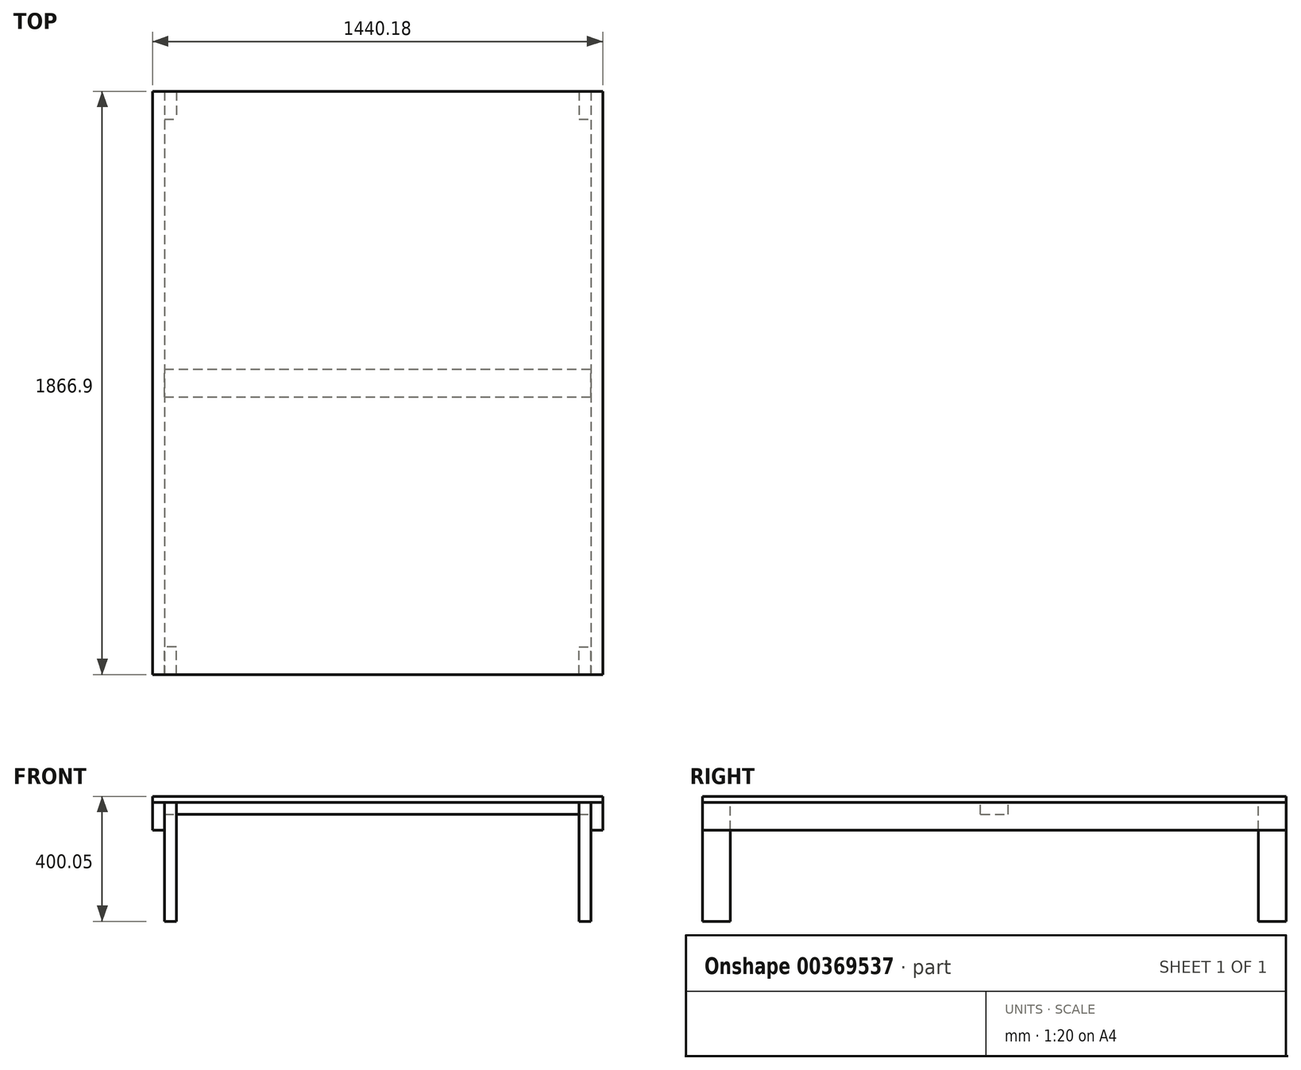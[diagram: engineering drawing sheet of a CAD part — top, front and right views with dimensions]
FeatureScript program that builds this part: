
annotation { "Feature Type Name" : "Feature", "Feature Type Description" : "" }
export const myFeature = defineFeature(function(context is Context, id is Id, definition is map)
    precondition{}
    {
        {
            var Q0;
            Q0=qCreatedBy(makeId("Top.planeOp"),FACE);
            var sketch = newSketch(context, id + "F0", { "sketchPlane" : qUnion([Q0])});
            skLineSegment(sketch, "E0.bottom", {"start": v(-720.1, 933.45) * mm, "end": v(720.1, 933.45) * mm});
            skLineSegment(sketch, "E0.top", {"start": v(-720.1, -933.45) * mm, "end": v(720.09, -933.45) * mm});
            skLineSegment(sketch, "E0.left", {"start": v(-720.1, 933.45) * mm, "end": v(-720.1, -933.45) * mm});
            skLineSegment(sketch, "E0.right", {"start": v(720.1, 933.45) * mm, "end": v(720.09, -933.45) * mm});
            skPoint(sketch, "E0.middle", {"position": v(0, 0) * mm});
            skSolve(sketch);
        }
        {
            var Q0;
            Q0 = qSketchRegion(id + "F0", true);
            extrude(context, id + "F1", {"entities" : qUnion([Q0]), "depth" : 19.05 * mm});
        }
        {
            var Q0;
            Q0=makeQuery(id+"F1.opExtrude","SWEPT_FACE",FACE,{"disambiguationData":[OSD([sQuery(id+"F0.wireOp",EDGE,"E0.top")])]});
            var sketch = newSketch(context, id + "F2", { "sketchPlane" : qUnion([Q0])});
            skLineSegment(sketch, "E1.bottom", {"start": v(720.09, 0) * mm, "end": v(681.99, 0) * mm});
            skLineSegment(sketch, "E1.top", {"start": v(720.09, -88.9) * mm, "end": v(681.99, -88.9) * mm});
            skLineSegment(sketch, "E1.left", {"start": v(720.09, 0) * mm, "end": v(720.09, -88.9) * mm});
            skLineSegment(sketch, "E1.right", {"start": v(681.99, 0) * mm, "end": v(681.99, -88.9) * mm});
            skLineSegment(sketch, "E2.bottom", {"start": v(-720.1, 0) * mm, "end": v(-682, 0) * mm});
            skLineSegment(sketch, "E2.top", {"start": v(-720.1, -88.9) * mm, "end": v(-682, -88.9) * mm});
            skLineSegment(sketch, "E2.left", {"start": v(-720.1, 0) * mm, "end": v(-720.1, -88.9) * mm});
            skLineSegment(sketch, "E2.right", {"start": v(-682, 0) * mm, "end": v(-682, -88.9) * mm});
            skSolve(sketch);
        }
        {
            var Q0;
            Q0 = qSketchRegion(id + "F2", true);
            var Q1;
            Q1=makeQuery(id+"F1.opExtrude","SWEPT_FACE",FACE,{"disambiguationData":[OSD([sQuery(id+"F0.wireOp",EDGE,"E0.bottom")])]});
            extrude(context, id + "F3", {"entities" : qUnion([Q0]), "endBound" : BoundingType.UP_TO_SURFACE, "oppositeDirection" : true, "endBoundEntityFace" : qUnion([Q1]), "depth" : 25.4 * mm});
        }
        {
            var Q0;
            Q0=makeQuery(id+"F1.opExtrude","CAP_FACE",FACE,{"disambiguationData":[OSD([sQuery(id+"F0.wireOp",EDGE,"E0.bottom"),sQuery(id+"F0.wireOp",EDGE,"E0.top"),sQuery(id+"F0.wireOp",EDGE,"E0.left"),sQuery(id+"F0.wireOp",EDGE,"E0.right")])],"isStart":true});
            var sketch = newSketch(context, id + "F4", { "sketchPlane" : qUnion([Q0])});
            skLineSegment(sketch, "E3.bottom", {"start": v(-643.9, 933.45) * mm, "end": v(-682, 933.45) * mm});
            skLineSegment(sketch, "E3.top", {"start": v(-643.9, 844.55) * mm, "end": v(-682, 844.55) * mm});
            skLineSegment(sketch, "E3.left", {"start": v(-643.9, 933.45) * mm, "end": v(-643.9, 844.55) * mm});
            skLineSegment(sketch, "E3.right", {"start": v(-682, 933.45) * mm, "end": v(-682, 844.55) * mm});
            skLineSegment(sketch, "E4.bottom", {"start": v(643.89, 933.45) * mm, "end": v(681.99, 933.45) * mm});
            skLineSegment(sketch, "E4.top", {"start": v(643.89, 844.55) * mm, "end": v(681.99, 844.55) * mm});
            skLineSegment(sketch, "E4.left", {"start": v(643.89, 933.45) * mm, "end": v(643.89, 844.55) * mm});
            skLineSegment(sketch, "E4.right", {"start": v(681.99, 933.45) * mm, "end": v(681.99, 844.55) * mm});
            skLineSegment(sketch, "E5.bottom", {"start": v(-682, -933.45) * mm, "end": v(-643.89, -933.45) * mm});
            skLineSegment(sketch, "E5.top", {"start": v(-682, -844.55) * mm, "end": v(-643.89, -844.55) * mm});
            skLineSegment(sketch, "E5.left", {"start": v(-682, -933.45) * mm, "end": v(-682, -844.55) * mm});
            skLineSegment(sketch, "E5.right", {"start": v(-643.89, -933.45) * mm, "end": v(-643.89, -844.55) * mm});
            skLineSegment(sketch, "E6.bottom", {"start": v(643.9, -933.45) * mm, "end": v(681.99, -933.45) * mm});
            skLineSegment(sketch, "E6.top", {"start": v(643.9, -844.55) * mm, "end": v(681.99, -844.55) * mm});
            skLineSegment(sketch, "E6.left", {"start": v(643.9, -933.45) * mm, "end": v(643.9, -844.55) * mm});
            skLineSegment(sketch, "E6.right", {"start": v(681.99, -933.45) * mm, "end": v(681.99, -844.55) * mm});
            skSolve(sketch);
        }
        {
            var Q0;
            Q0 = qSketchRegion(id + "F4", true);
            extrude(context, id + "F5", {"entities" : qUnion([Q0]), "depth" : 381 * mm});
        }
        {
            var Q0;
            Q0=makeQuery(id+"F1.opExtrude","CAP_FACE",FACE,{"disambiguationData":[OSD([sQuery(id+"F0.wireOp",EDGE,"E0.bottom"),sQuery(id+"F0.wireOp",EDGE,"E0.top"),sQuery(id+"F0.wireOp",EDGE,"E0.left"),sQuery(id+"F0.wireOp",EDGE,"E0.right")])],"isStart":true});
            var sketch = newSketch(context, id + "F6", { "sketchPlane" : qUnion([Q0])});
            skLineSegment(sketch, "E7.bottom", {"start": v(-682, 44.45) * mm, "end": v(682, 44.45) * mm});
            skLineSegment(sketch, "E7.top", {"start": v(-682, -44.45) * mm, "end": v(682, -44.45) * mm});
            skLineSegment(sketch, "E7.left", {"start": v(-682, 44.45) * mm, "end": v(-682, -44.45) * mm});
            skLineSegment(sketch, "E7.right", {"start": v(682, 44.45) * mm, "end": v(682, -44.45) * mm});
            skPoint(sketch, "E7.middle", {"position": v(0, 0) * mm});
            skSolve(sketch);
        }
        {
            var Q0;
            Q0 = qSketchRegion(id + "F6", true);
            extrude(context, id + "F7", {"entities" : qUnion([Q0]), "depth" : 38.1 * mm});
        }
    });
